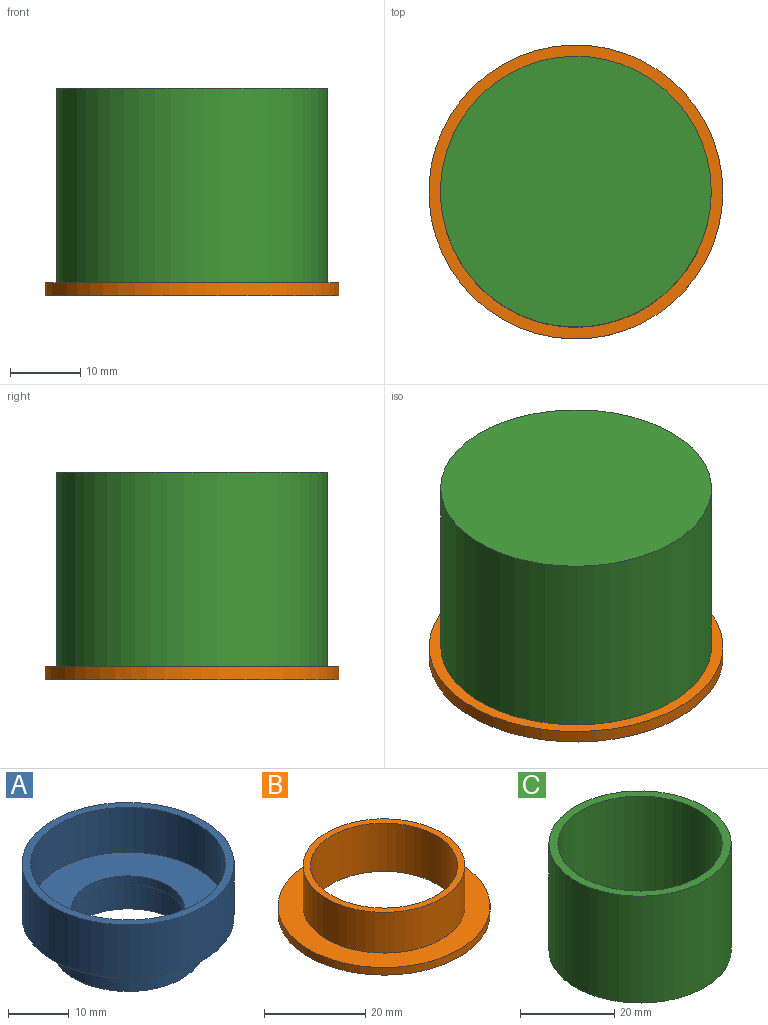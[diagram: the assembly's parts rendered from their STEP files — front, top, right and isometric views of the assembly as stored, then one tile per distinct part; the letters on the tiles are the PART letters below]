
ASSEMBLY  parts=3 mates=2
PART A: 10 faces, bbox 34.8x34.8x16.8 mm
  f0: plane 21.92x21.92mm, normal (0,0,-1), area 107.4mm2, adj f1,f7
  f1: cylinder r=9.27mm len=18.54mm, axis (0,0,-1), area 100.6mm2, adj f0,f3
  f2: cylinder r=17.4mm len=34.8mm, axis (0,0,-1), area 1174.6mm2, adj f4,f6
  f3: plane 32x32mm, normal (0,0,1), area 534.4mm2, adj f1,f5
  f4: plane 34.8x34.8mm, normal (0,0,-1), area 458.4mm2, adj f2,f8
  f5: cylinder r=16mm len=32mm, axis (0,0,-1), area 906.6mm2, adj f3,f6
  f6: plane 34.8x34.8mm, normal (0,0,1), area 146.6mm2, adj f2,f5
  f7: cylinder r=10.96mm len=21.92mm, axis (0,0,1), area 419.8mm2, adj f0,f9
  f8: cylinder r=12.52mm len=25.04mm, axis (0,0,1), area 479.6mm2, adj f4,f9
  f9: plane 25.04x25.04mm, normal (0,0,-1), area 115.2mm2, adj f7,f8
PART B: 6 faces, bbox 41.9x41.9x11.7 mm
  f0: cylinder r=14.54mm len=29.08mm, axis (0,0,-1), area 1067.5mm2, adj f2,f4
  f1: cylinder r=16mm len=32mm, axis (0,0,-1), area 990.9mm2, adj f2,f5
  f2: plane 32x32mm, normal (0,0,1), area 140.1mm2, adj f0,f1
  f3: cylinder r=20.96mm len=41.91mm, axis (0,0,1), area 240.8mm2, adj f4,f5
  f4: plane 41.91x41.91mm, normal (0,0,-1), area 715.2mm2, adj f0,f3
  f5: plane 41.91x41.91mm, normal (0,0,1), area 575.1mm2, adj f1,f3
PART C: 5 faces, bbox 38.6x38.6x27.7 mm
  f0: cylinder r=19.3mm len=38.61mm, axis (0,0,1), area 3358.1mm2, adj f1,f3
  f1: plane 38.61x38.61mm, normal (0,0,-1), area 1170.7mm2, adj f0
  f2: cylinder r=17.4mm len=34.8mm, axis (0,0,-1), area 2749mm2, adj f3,f4
  f3: plane 38.61x38.61mm, normal (0,0,1), area 219.7mm2, adj f0,f2
  f4: plane 34.8x34.8mm, normal (0,0,1), area 951mm2, adj f2
PLACE A rot(axis=(1,0,0),180deg) t=(0,0,11.58)mm
PLACE B at identity fixed
PLACE C rot(axis=(1,0,0),180deg) t=(0,0,25.15)mm
MATE fastened A.f1 <-> B.f0  axis (0,0,-1) through (0,0,9.86)mm
MATE fastened C.f2 <-> B.f3  axis (0,0,1) through (0,0,0)mm
